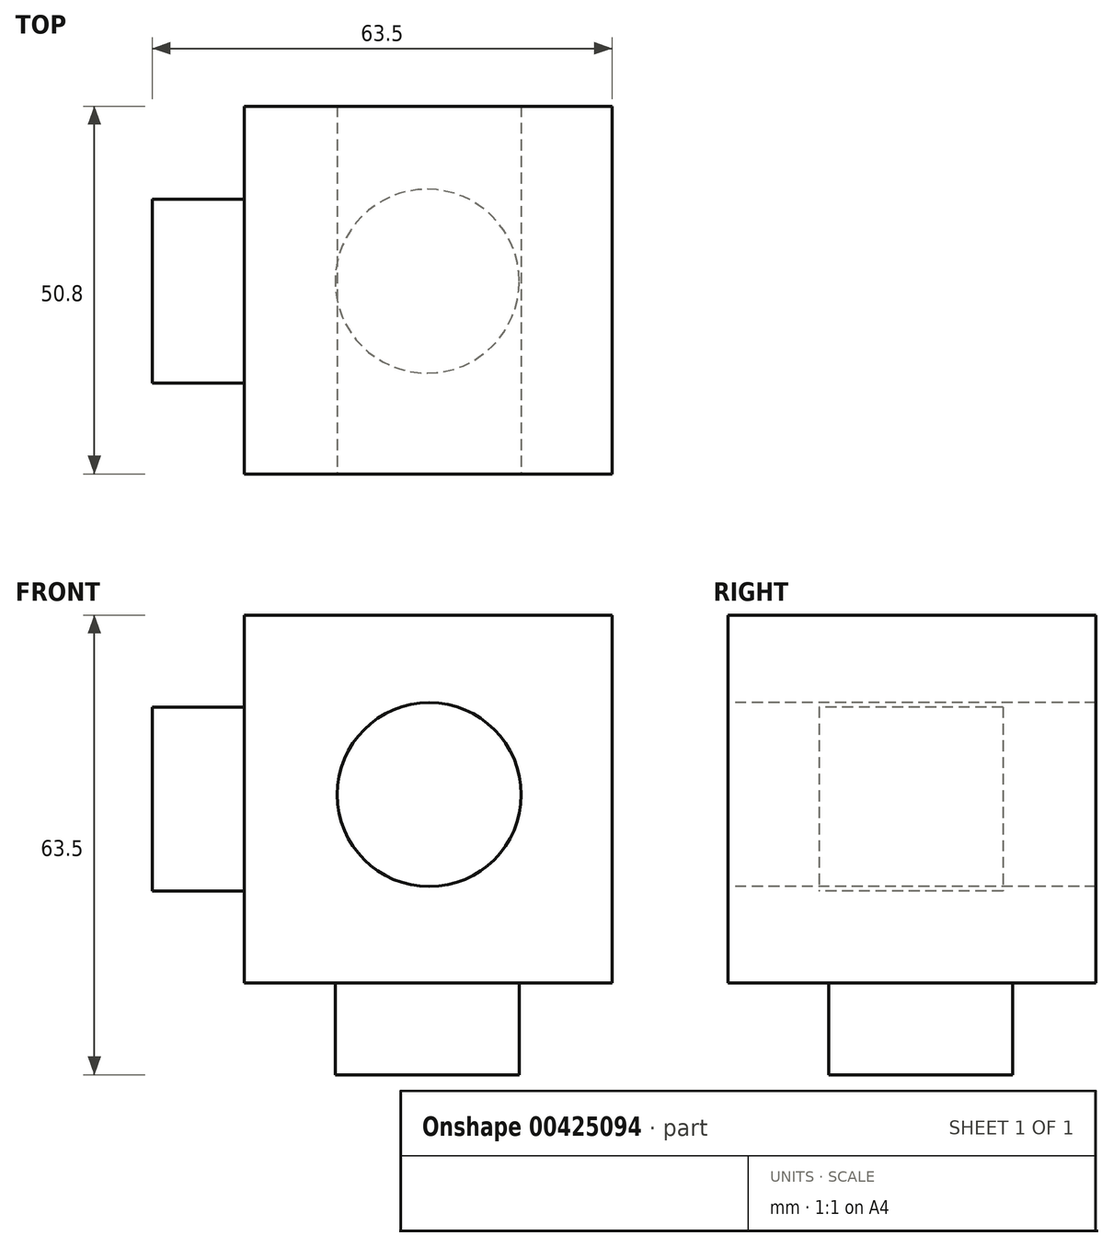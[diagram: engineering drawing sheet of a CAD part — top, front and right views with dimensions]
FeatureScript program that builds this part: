
annotation { "Feature Type Name" : "Feature", "Feature Type Description" : "" }
export const myFeature = defineFeature(function(context is Context, id is Id, definition is map)
    precondition{}
    {
        {
            var Q0;
            Q0=qCreatedBy(makeId("Front.planeOp"),FACE);
            var sketch = newSketch(context, id + "F0", { "sketchPlane" : qUnion([Q0])});
            skLineSegment(sketch, "E0.bottom", {"start": v(0, 0) * mm, "end": v(50.8, 0) * mm});
            skLineSegment(sketch, "E0.top", {"start": v(0, 50.8) * mm, "end": v(50.8, 50.8) * mm});
            skLineSegment(sketch, "E0.left", {"start": v(0, 0) * mm, "end": v(0, 50.8) * mm});
            skLineSegment(sketch, "E0.right", {"start": v(50.8, 0) * mm, "end": v(50.8, 50.8) * mm});
            skSolve(sketch);
        }
        {
            var Q0;
            Q0 = qSketchRegion(id + "F0", true);
            extrude(context, id + "F1", {"entities" : qUnion([Q0]), "depth" : 50.8 * mm});
        }
        {
            var Q0;
            Q0=makeQuery(id+"F1.opExtrude","CAP_FACE",FACE,{"disambiguationData":[OSD([sQuery(id+"F0.wireOp",EDGE,"E0.bottom"),sQuery(id+"F0.wireOp",EDGE,"E0.top"),sQuery(id+"F0.wireOp",EDGE,"E0.left"),sQuery(id+"F0.wireOp",EDGE,"E0.right")])],"isStart":false});
            var sketch = newSketch(context, id + "F2", { "sketchPlane" : qUnion([Q0])});
            skCircle(sketch, "E1", {"center": v(25.54, 26) * mm, "radius": 12.7 * mm});
            skSolve(sketch);
        }
        {
            var Q0;
            Q0 = qSketchRegion(id + "F2", true);
            extrude(context, id + "F3", {"entities" : qUnion([Q0]), "operationType" : NewBodyOperationType.REMOVE, "oppositeDirection" : true, "depth" : 100.08 * mm});
        }
        {
            var Q0;
            Q0=makeQuery(id+"F1.opExtrude","SWEPT_FACE",FACE,{"disambiguationData":[OSD([sQuery(id+"F0.wireOp",EDGE,"E0.left")])]});
            var sketch = newSketch(context, id + "F4", { "sketchPlane" : qUnion([Q0])});
            skLineSegment(sketch, "E2.bottom", {"start": v(12.83, 38.08) * mm, "end": v(38.23, 38.08) * mm});
            skLineSegment(sketch, "E2.top", {"start": v(12.83, 12.68) * mm, "end": v(38.23, 12.68) * mm});
            skLineSegment(sketch, "E2.left", {"start": v(12.83, 38.08) * mm, "end": v(12.83, 12.68) * mm});
            skLineSegment(sketch, "E2.right", {"start": v(38.23, 38.08) * mm, "end": v(38.23, 12.68) * mm});
            skSolve(sketch);
        }
        {
            var Q0;
            Q0=makeQuery(id+"F1.opExtrude","SWEPT_FACE",FACE,{"disambiguationData":[OSD([sQuery(id+"F0.wireOp",EDGE,"E0.bottom")])]});
            var sketch = newSketch(context, id + "F5", { "sketchPlane" : qUnion([Q0])});
            skCircle(sketch, "E3", {"center": v(25.25, 24.19) * mm, "radius": 12.7 * mm});
            skSolve(sketch);
        }
        {
            var Q0;
            Q0=makeQuery(id+"F5.imprint","IMPRINT",FACE,{"disambiguationData":[TD([[makeQuery(id+"F5.imprint","IMPRINT",EDGE,{"derivedFrom":sQuery(id+"F5.wireOp",EDGE,"E3")}),1.0]])]});
            extrude(context, id + "F6", {"entities" : qUnion([Q0]), "operationType" : NewBodyOperationType.ADD, "depth" : 12.7 * mm});
        }
        {
            var Q0;
            Q0=makeQuery(id+"F4.imprint","IMPRINT",FACE,{"disambiguationData":[TD([[makeQuery(id+"F4.imprint","IMPRINT",EDGE,{"derivedFrom":sQuery(id+"F4.wireOp",EDGE,"E2.bottom")}),-1.0]])]});
            extrude(context, id + "F7", {"entities" : qUnion([Q0]), "operationType" : NewBodyOperationType.ADD, "depth" : 12.7 * mm});
        }
    });
